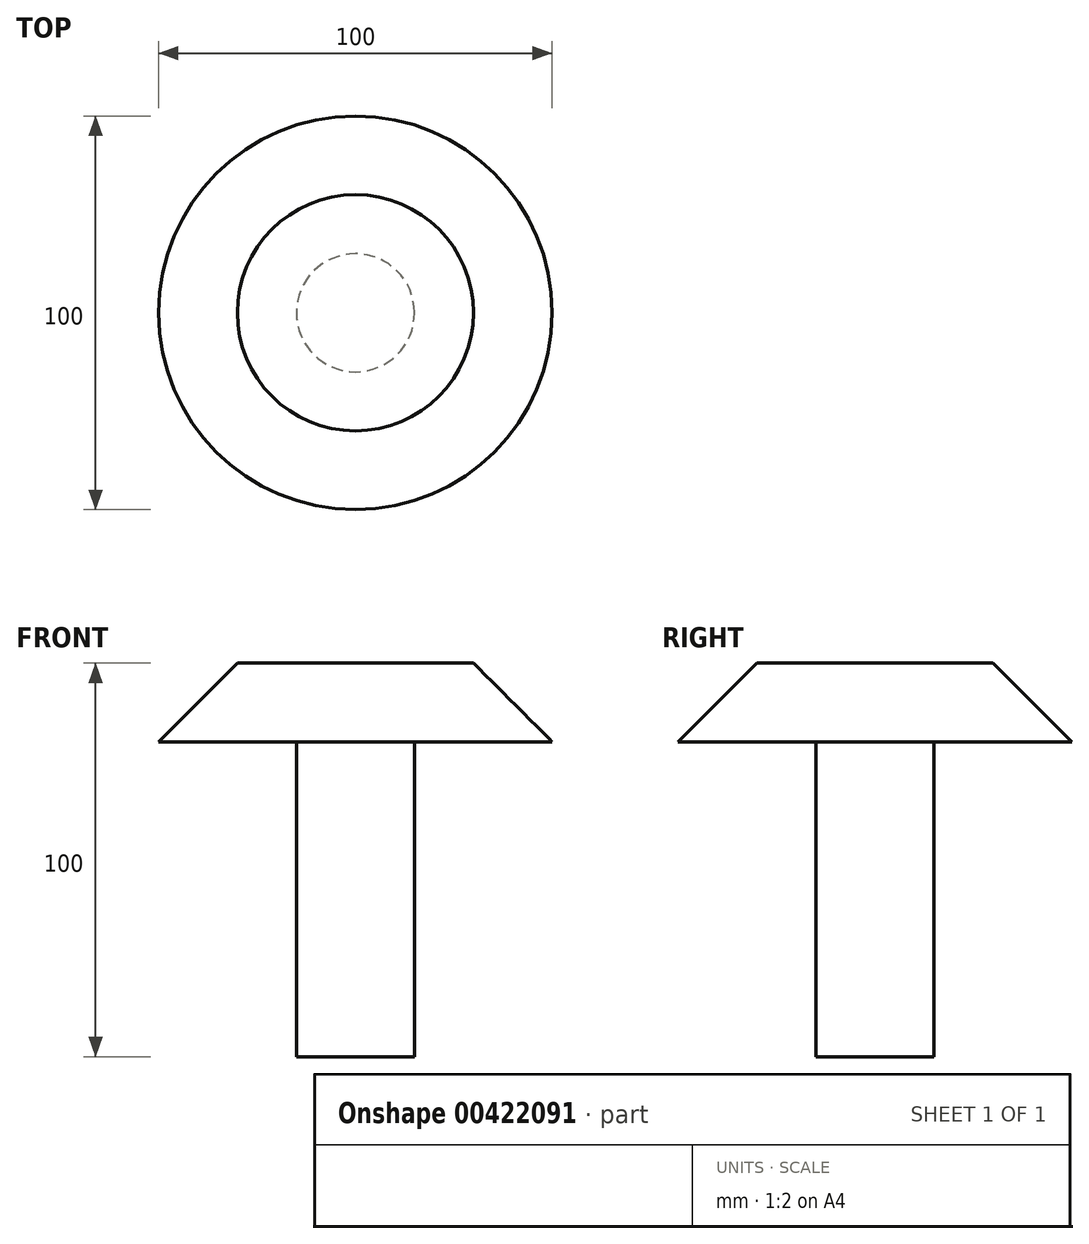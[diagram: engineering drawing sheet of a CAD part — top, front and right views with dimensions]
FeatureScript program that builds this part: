
annotation { "Feature Type Name" : "Feature", "Feature Type Description" : "" }
export const myFeature = defineFeature(function(context is Context, id is Id, definition is map)
    precondition{}
    {
        {
            var Q0;
            Q0=qCreatedBy(makeId("Top.planeOp"),FACE);
            var sketch = newSketch(context, id + "F0", { "sketchPlane" : qUnion([Q0])});
            skCircle(sketch, "E0", {"center": v(0, 0) * mm, "radius": 50 * mm});
            skSolve(sketch);
        }
        {
            var Q0;
            Q0=makeQuery(id+"F0.imprint","IMPRINT",FACE,{"disambiguationData":[TD([[makeQuery(id+"F0.imprint","IMPRINT",EDGE,{"derivedFrom":sQuery(id+"F0.wireOp",EDGE,"E0")}),1.0]])]});
            var Q1;
            Q1=sQuery(id+"F0.wireOp",EDGE,"E0");
            extrude(context, id + "F1", {"entities" : qUnion([Q0]), "surfaceEntities" : qUnion([Q1]), "depth" : 20 * mm, "hasDraft" : true, "draftAngle" : 45 * degree, "draftPullDirection" : true});
        }
        {
            var Q0;
            Q0=makeQuery(id+"F1.opExtrude","CAP_FACE",FACE,{"disambiguationData":[OSD([sQuery(id+"F0.wireOp",EDGE,"E0")])],"isStart":true});
            var sketch = newSketch(context, id + "F2", { "sketchPlane" : qUnion([Q0])});
            skCircle(sketch, "E1", {"center": v(0, 0) * mm, "radius": 15 * mm});
            skSolve(sketch);
        }
        {
            var Q0;
            Q0=makeQuery(id+"F2.imprint","IMPRINT",FACE,{"disambiguationData":[TD([[makeQuery(id+"F2.imprint","IMPRINT",EDGE,{"derivedFrom":sQuery(id+"F2.wireOp",EDGE,"E1")}),1.0]])]});
            extrude(context, id + "F3", {"entities" : qUnion([Q0]), "operationType" : NewBodyOperationType.ADD, "depth" : 80 * mm});
        }
    });
